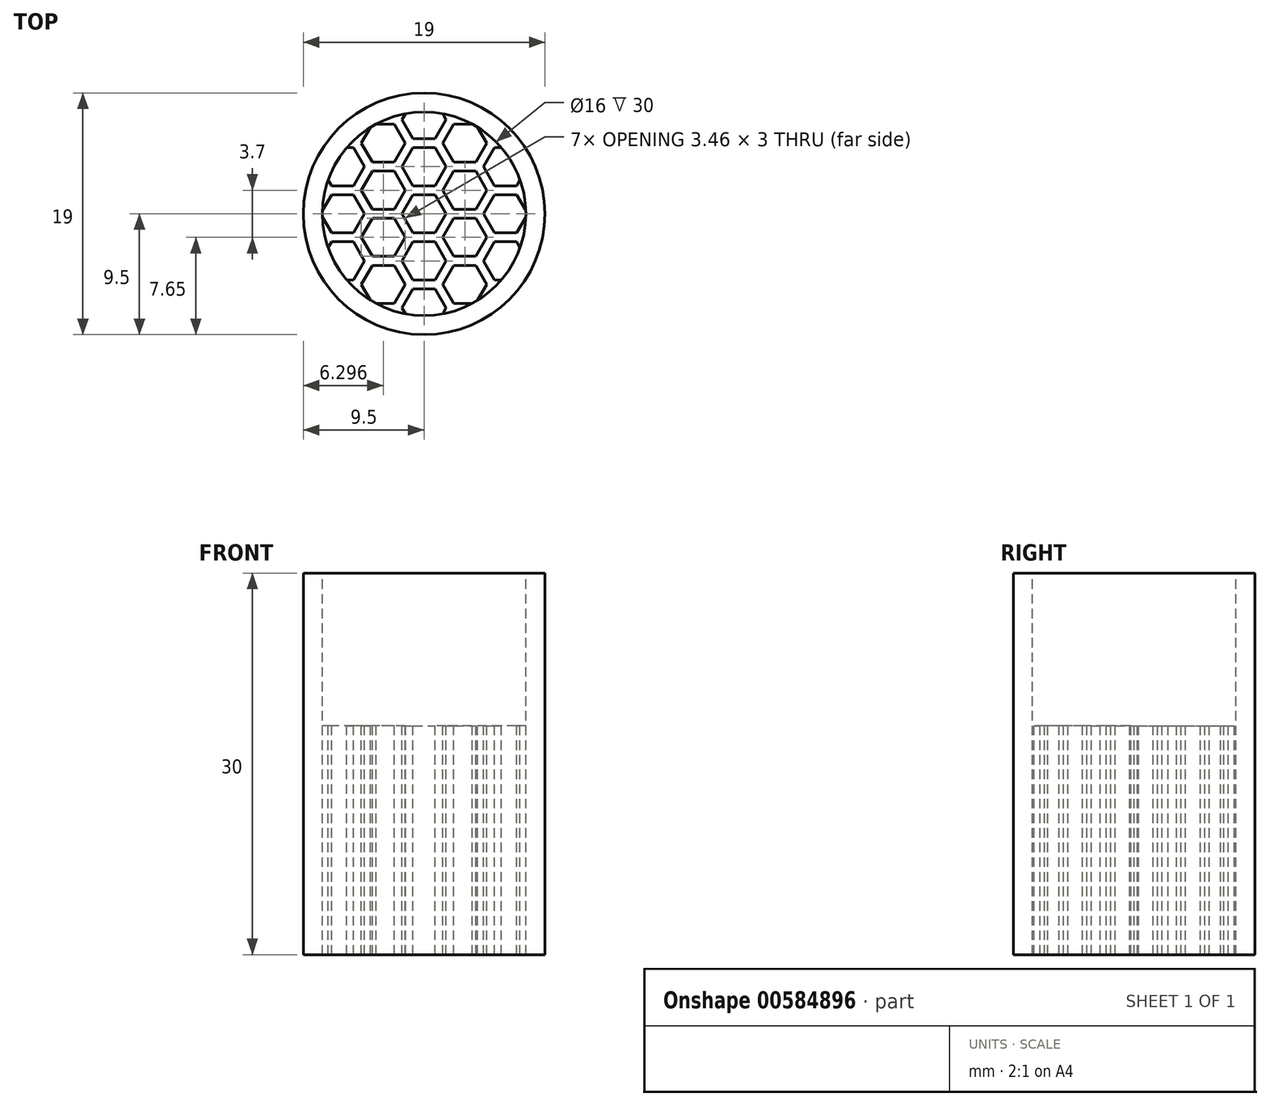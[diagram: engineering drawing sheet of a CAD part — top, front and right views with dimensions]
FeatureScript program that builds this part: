
annotation { "Feature Type Name" : "Feature", "Feature Type Description" : "" }
export const myFeature = defineFeature(function(context is Context, id is Id, definition is map)
    precondition{}
    {
        {
            var Q0;
            Q0=qCreatedBy(makeId("Top.planeOp"),FACE);
            var sketch = newSketch(context, id + "F0", { "sketchPlane" : qUnion([Q0])});
            skCircle(sketch, "E0", {"center": v(0, 0) * mm, "radius": 9.5 * mm});
            skCircle(sketch, "E1", {"center": v(0, 0) * mm, "radius": 8 * mm});
            skCircle(sketch, "E2.cCircle", {"center": v(0, 0) * mm, "radius": 1.5 * mm, "construction": true});
            skLineSegment(sketch, "E2.0", {"start": v(1.73, 0) * mm, "end": v(0.87, -1.5) * mm});
            skLineSegment(sketch, "E2.1", {"start": v(0.87, -1.5) * mm, "end": v(-0.87, -1.5) * mm});
            skLineSegment(sketch, "E2.2", {"start": v(-0.87, -1.5) * mm, "end": v(-1.73, 0) * mm});
            skLineSegment(sketch, "E2.3", {"start": v(-1.73, 0) * mm, "end": v(-0.87, 1.5) * mm});
            skLineSegment(sketch, "E2.4", {"start": v(-0.87, 1.5) * mm, "end": v(0.87, 1.5) * mm});
            skLineSegment(sketch, "E2.5", {"start": v(0.87, 1.5) * mm, "end": v(1.73, 0) * mm});
            skPoint(sketch, "E2.0.midPoint", {"position": v(1.3, -0.75) * mm});
            skCircle(sketch, "E3.cCircle", {"center": v(0, 0) * mm, "radius": 1.85 * mm, "construction": true});
            skLineSegment(sketch, "E3.0", {"start": v(2.14, 0) * mm, "end": v(1.07, -1.85) * mm});
            skLineSegment(sketch, "E3.1", {"start": v(1.07, -1.85) * mm, "end": v(-1.07, -1.85) * mm});
            skLineSegment(sketch, "E3.2", {"start": v(-1.07, -1.85) * mm, "end": v(-2.14, 0) * mm});
            skLineSegment(sketch, "E3.3", {"start": v(-2.14, 0) * mm, "end": v(-1.07, 1.85) * mm});
            skLineSegment(sketch, "E3.4", {"start": v(-1.07, 1.85) * mm, "end": v(1.07, 1.85) * mm});
            skLineSegment(sketch, "E3.5", {"start": v(1.07, 1.85) * mm, "end": v(2.14, 0) * mm});
            skPoint(sketch, "E3.0.midPoint", {"position": v(1.6, -0.92) * mm});
            skCircle(sketch, "E4.cCircle", {"center": v(0, 3.7) * mm, "radius": 1.5 * mm, "construction": true});
            skLineSegment(sketch, "E4.0", {"start": v(1.73, 3.7) * mm, "end": v(0.87, 2.2) * mm});
            skLineSegment(sketch, "E4.1", {"start": v(0.87, 2.2) * mm, "end": v(-0.87, 2.2) * mm});
            skLineSegment(sketch, "E4.2", {"start": v(-0.87, 2.2) * mm, "end": v(-1.73, 3.7) * mm});
            skLineSegment(sketch, "E4.3", {"start": v(-1.73, 3.7) * mm, "end": v(-0.87, 5.2) * mm});
            skLineSegment(sketch, "E4.4", {"start": v(-0.87, 5.2) * mm, "end": v(0.87, 5.2) * mm});
            skLineSegment(sketch, "E4.5", {"start": v(0.87, 5.2) * mm, "end": v(1.73, 3.7) * mm});
            skPoint(sketch, "E4.0.midPoint", {"position": v(1.3, 2.95) * mm});
            skCircle(sketch, "E5.cCircle", {"center": v(0, 3.7) * mm, "radius": 1.85 * mm, "construction": true});
            skLineSegment(sketch, "E5.0", {"start": v(2.14, 3.7) * mm, "end": v(1.07, 1.85) * mm});
            skLineSegment(sketch, "E5.1", {"start": v(1.07, 1.85) * mm, "end": v(-1.07, 1.85) * mm});
            skLineSegment(sketch, "E5.2", {"start": v(-1.07, 1.85) * mm, "end": v(-2.14, 3.7) * mm});
            skLineSegment(sketch, "E5.3", {"start": v(-2.14, 3.7) * mm, "end": v(-1.07, 5.55) * mm});
            skLineSegment(sketch, "E5.4", {"start": v(-1.07, 5.55) * mm, "end": v(1.07, 5.55) * mm});
            skLineSegment(sketch, "E5.5", {"start": v(1.07, 5.55) * mm, "end": v(2.14, 3.7) * mm});
            skPoint(sketch, "E5.0.midPoint", {"position": v(1.6, 2.77) * mm});
            skCircle(sketch, "E6.cCircle", {"center": v(3.2, 1.85) * mm, "radius": 1.5 * mm, "construction": true});
            skLineSegment(sketch, "E6.0", {"start": v(4.94, 1.85) * mm, "end": v(4.07, 0.35) * mm});
            skLineSegment(sketch, "E6.1", {"start": v(4.07, 0.35) * mm, "end": v(2.34, 0.35) * mm});
            skLineSegment(sketch, "E6.2", {"start": v(2.34, 0.35) * mm, "end": v(1.47, 1.85) * mm});
            skLineSegment(sketch, "E6.3", {"start": v(1.47, 1.85) * mm, "end": v(2.34, 3.35) * mm});
            skLineSegment(sketch, "E6.4", {"start": v(2.34, 3.35) * mm, "end": v(4.07, 3.35) * mm});
            skLineSegment(sketch, "E6.5", {"start": v(4.07, 3.35) * mm, "end": v(4.94, 1.85) * mm});
            skPoint(sketch, "E6.0.midPoint", {"position": v(4.5, 1.1) * mm});
            skCircle(sketch, "E7.cCircle", {"center": v(3.2, 1.85) * mm, "radius": 1.85 * mm, "construction": true});
            skLineSegment(sketch, "E7.0", {"start": v(5.34, 1.85) * mm, "end": v(4.27, 0) * mm});
            skLineSegment(sketch, "E7.1", {"start": v(4.27, 0) * mm, "end": v(2.14, 0) * mm});
            skLineSegment(sketch, "E7.2", {"start": v(2.14, 0) * mm, "end": v(1.07, 1.85) * mm});
            skLineSegment(sketch, "E7.3", {"start": v(1.07, 1.85) * mm, "end": v(2.14, 3.7) * mm});
            skLineSegment(sketch, "E7.4", {"start": v(2.14, 3.7) * mm, "end": v(4.27, 3.7) * mm});
            skLineSegment(sketch, "E7.5", {"start": v(4.27, 3.7) * mm, "end": v(5.34, 1.85) * mm});
            skPoint(sketch, "E7.0.midPoint", {"position": v(4.8, 0.93) * mm});
            skCircle(sketch, "E8.cCircle", {"center": v(3.2, -1.85) * mm, "radius": 1.5 * mm, "construction": true});
            skLineSegment(sketch, "E8.0", {"start": v(4.07, -3.35) * mm, "end": v(2.34, -3.35) * mm});
            skLineSegment(sketch, "E8.1", {"start": v(2.34, -3.35) * mm, "end": v(1.47, -1.85) * mm});
            skLineSegment(sketch, "E8.2", {"start": v(1.47, -1.85) * mm, "end": v(2.34, -0.35) * mm});
            skLineSegment(sketch, "E8.3", {"start": v(2.34, -0.35) * mm, "end": v(4.07, -0.35) * mm});
            skLineSegment(sketch, "E8.4", {"start": v(4.07, -0.35) * mm, "end": v(4.94, -1.85) * mm});
            skLineSegment(sketch, "E8.5", {"start": v(4.94, -1.85) * mm, "end": v(4.07, -3.35) * mm});
            skPoint(sketch, "E8.0.midPoint", {"position": v(3.2, -3.35) * mm});
            skCircle(sketch, "E9.cCircle", {"center": v(3.2, -1.85) * mm, "radius": 1.85 * mm, "construction": true});
            skLineSegment(sketch, "E9.0", {"start": v(4.27, -3.7) * mm, "end": v(2.14, -3.7) * mm});
            skLineSegment(sketch, "E9.1", {"start": v(2.14, -3.7) * mm, "end": v(1.07, -1.85) * mm});
            skLineSegment(sketch, "E9.2", {"start": v(1.07, -1.85) * mm, "end": v(2.14, 0) * mm});
            skLineSegment(sketch, "E9.3", {"start": v(2.14, 0) * mm, "end": v(4.27, 0) * mm});
            skLineSegment(sketch, "E9.4", {"start": v(4.27, 0) * mm, "end": v(5.34, -1.85) * mm});
            skLineSegment(sketch, "E9.5", {"start": v(5.34, -1.85) * mm, "end": v(4.27, -3.7) * mm});
            skPoint(sketch, "E9.0.midPoint", {"position": v(3.2, -3.7) * mm});
            skCircle(sketch, "E10.cCircle", {"center": v(0, -3.7) * mm, "radius": 1.5 * mm, "construction": true});
            skLineSegment(sketch, "E10.0", {"start": v(-1.73, -3.7) * mm, "end": v(-0.87, -2.2) * mm});
            skLineSegment(sketch, "E10.1", {"start": v(-0.87, -2.2) * mm, "end": v(0.87, -2.2) * mm});
            skLineSegment(sketch, "E10.2", {"start": v(0.87, -2.2) * mm, "end": v(1.73, -3.7) * mm});
            skLineSegment(sketch, "E10.3", {"start": v(1.73, -3.7) * mm, "end": v(0.87, -5.2) * mm});
            skLineSegment(sketch, "E10.4", {"start": v(0.87, -5.2) * mm, "end": v(-0.87, -5.2) * mm});
            skLineSegment(sketch, "E10.5", {"start": v(-0.87, -5.2) * mm, "end": v(-1.73, -3.7) * mm});
            skPoint(sketch, "E10.0.midPoint", {"position": v(-1.3, -2.95) * mm});
            skCircle(sketch, "E11.cCircle", {"center": v(0, -3.7) * mm, "radius": 1.85 * mm, "construction": true});
            skLineSegment(sketch, "E11.0", {"start": v(-2.14, -3.7) * mm, "end": v(-1.07, -1.85) * mm});
            skLineSegment(sketch, "E11.1", {"start": v(-1.07, -1.85) * mm, "end": v(1.07, -1.85) * mm});
            skLineSegment(sketch, "E11.2", {"start": v(1.07, -1.85) * mm, "end": v(2.14, -3.7) * mm});
            skLineSegment(sketch, "E11.3", {"start": v(2.14, -3.7) * mm, "end": v(1.07, -5.55) * mm});
            skLineSegment(sketch, "E11.4", {"start": v(1.07, -5.55) * mm, "end": v(-1.07, -5.55) * mm});
            skLineSegment(sketch, "E11.5", {"start": v(-1.07, -5.55) * mm, "end": v(-2.14, -3.7) * mm});
            skPoint(sketch, "E11.0.midPoint", {"position": v(-1.6, -2.78) * mm});
            skCircle(sketch, "E12.cCircle", {"center": v(-3.2, -1.85) * mm, "radius": 1.5 * mm, "construction": true});
            skLineSegment(sketch, "E12.0", {"start": v(-4.07, -0.35) * mm, "end": v(-2.34, -0.35) * mm});
            skLineSegment(sketch, "E12.1", {"start": v(-2.34, -0.35) * mm, "end": v(-1.47, -1.85) * mm});
            skLineSegment(sketch, "E12.2", {"start": v(-1.47, -1.85) * mm, "end": v(-2.34, -3.35) * mm});
            skLineSegment(sketch, "E12.3", {"start": v(-2.34, -3.35) * mm, "end": v(-4.07, -3.35) * mm});
            skLineSegment(sketch, "E12.4", {"start": v(-4.07, -3.35) * mm, "end": v(-4.94, -1.85) * mm});
            skLineSegment(sketch, "E12.5", {"start": v(-4.94, -1.85) * mm, "end": v(-4.07, -0.35) * mm});
            skPoint(sketch, "E12.0.midPoint", {"position": v(-3.2, -0.35) * mm});
            skCircle(sketch, "E13.cCircle", {"center": v(-3.2, -1.85) * mm, "radius": 1.85 * mm, "construction": true});
            skLineSegment(sketch, "E13.0", {"start": v(-4.27, 0) * mm, "end": v(-2.14, 0) * mm});
            skLineSegment(sketch, "E13.1", {"start": v(-2.14, 0) * mm, "end": v(-1.07, -1.85) * mm});
            skLineSegment(sketch, "E13.2", {"start": v(-1.07, -1.85) * mm, "end": v(-2.14, -3.7) * mm});
            skLineSegment(sketch, "E13.3", {"start": v(-2.14, -3.7) * mm, "end": v(-4.27, -3.7) * mm});
            skLineSegment(sketch, "E13.4", {"start": v(-4.27, -3.7) * mm, "end": v(-5.34, -1.85) * mm});
            skLineSegment(sketch, "E13.5", {"start": v(-5.34, -1.85) * mm, "end": v(-4.27, 0) * mm});
            skPoint(sketch, "E13.0.midPoint", {"position": v(-3.2, 0) * mm});
            skCircle(sketch, "E14.cCircle", {"center": v(-3.2, 1.85) * mm, "radius": 1.5 * mm, "construction": true});
            skLineSegment(sketch, "E14.0", {"start": v(-2.34, 3.35) * mm, "end": v(-1.47, 1.85) * mm});
            skLineSegment(sketch, "E14.1", {"start": v(-1.47, 1.85) * mm, "end": v(-2.34, 0.35) * mm});
            skLineSegment(sketch, "E14.2", {"start": v(-2.34, 0.35) * mm, "end": v(-4.07, 0.35) * mm});
            skLineSegment(sketch, "E14.3", {"start": v(-4.07, 0.35) * mm, "end": v(-4.94, 1.85) * mm});
            skLineSegment(sketch, "E14.4", {"start": v(-4.94, 1.85) * mm, "end": v(-4.07, 3.35) * mm});
            skLineSegment(sketch, "E14.5", {"start": v(-4.07, 3.35) * mm, "end": v(-2.34, 3.35) * mm});
            skPoint(sketch, "E14.0.midPoint", {"position": v(-1.9, 2.6) * mm});
            skCircle(sketch, "E15.cCircle", {"center": v(-3.2, 1.85) * mm, "radius": 1.85 * mm, "construction": true});
            skLineSegment(sketch, "E15.0", {"start": v(-2.14, 3.7) * mm, "end": v(-1.07, 1.85) * mm});
            skLineSegment(sketch, "E15.1", {"start": v(-1.07, 1.85) * mm, "end": v(-2.14, 0) * mm});
            skLineSegment(sketch, "E15.2", {"start": v(-2.14, 0) * mm, "end": v(-4.27, 0) * mm});
            skLineSegment(sketch, "E15.3", {"start": v(-4.27, 0) * mm, "end": v(-5.34, 1.85) * mm});
            skLineSegment(sketch, "E15.4", {"start": v(-5.34, 1.85) * mm, "end": v(-4.27, 3.7) * mm});
            skLineSegment(sketch, "E15.5", {"start": v(-4.27, 3.7) * mm, "end": v(-2.14, 3.7) * mm});
            skPoint(sketch, "E15.0.midPoint", {"position": v(-1.6, 2.77) * mm});
            skCircle(sketch, "E16.cCircle", {"center": v(3.2, 5.55) * mm, "radius": 1.5 * mm, "construction": true});
            skLineSegment(sketch, "E16.0", {"start": v(4.94, 5.55) * mm, "end": v(4.07, 4.05) * mm});
            skLineSegment(sketch, "E16.1", {"start": v(4.07, 4.05) * mm, "end": v(2.34, 4.05) * mm});
            skLineSegment(sketch, "E16.2", {"start": v(2.34, 4.05) * mm, "end": v(1.47, 5.55) * mm});
            skLineSegment(sketch, "E16.3", {"start": v(1.47, 5.55) * mm, "end": v(2.34, 7.05) * mm});
            skLineSegment(sketch, "E16.4", {"start": v(2.34, 7.05) * mm, "end": v(4.07, 7.05) * mm});
            skLineSegment(sketch, "E16.5", {"start": v(4.07, 7.05) * mm, "end": v(4.94, 5.55) * mm});
            skPoint(sketch, "E16.0.midPoint", {"position": v(4.5, 4.8) * mm});
            skCircle(sketch, "E17.cCircle", {"center": v(3.2, 5.55) * mm, "radius": 1.85 * mm, "construction": true});
            skLineSegment(sketch, "E17.0", {"start": v(5.34, 5.55) * mm, "end": v(4.27, 3.7) * mm});
            skLineSegment(sketch, "E17.1", {"start": v(4.27, 3.7) * mm, "end": v(2.14, 3.7) * mm});
            skLineSegment(sketch, "E17.2", {"start": v(2.14, 3.7) * mm, "end": v(1.07, 5.55) * mm});
            skLineSegment(sketch, "E17.3", {"start": v(1.07, 5.55) * mm, "end": v(2.14, 7.4) * mm});
            skLineSegment(sketch, "E17.4", {"start": v(2.14, 7.4) * mm, "end": v(4.27, 7.4) * mm});
            skLineSegment(sketch, "E17.5", {"start": v(4.27, 7.4) * mm, "end": v(5.34, 5.55) * mm});
            skPoint(sketch, "E17.0.midPoint", {"position": v(4.8, 4.63) * mm});
            skCircle(sketch, "E18.cCircle", {"center": v(0, 7.4) * mm, "radius": 1.5 * mm, "construction": true});
            skLineSegment(sketch, "E18.0", {"start": v(1.73, 7.4) * mm, "end": v(0.87, 5.9) * mm});
            skLineSegment(sketch, "E18.1", {"start": v(0.87, 5.9) * mm, "end": v(-0.87, 5.9) * mm});
            skLineSegment(sketch, "E18.2", {"start": v(-0.87, 5.9) * mm, "end": v(-1.73, 7.4) * mm});
            skLineSegment(sketch, "E18.3", {"start": v(-1.73, 7.4) * mm, "end": v(-0.87, 8.9) * mm});
            skLineSegment(sketch, "E18.4", {"start": v(-0.87, 8.9) * mm, "end": v(0.87, 8.9) * mm});
            skLineSegment(sketch, "E18.5", {"start": v(0.87, 8.9) * mm, "end": v(1.73, 7.4) * mm});
            skPoint(sketch, "E18.0.midPoint", {"position": v(1.3, 6.65) * mm});
            skCircle(sketch, "E19.cCircle", {"center": v(0, 7.4) * mm, "radius": 1.85 * mm, "construction": true});
            skLineSegment(sketch, "E19.0", {"start": v(2.14, 7.4) * mm, "end": v(1.07, 5.55) * mm});
            skLineSegment(sketch, "E19.1", {"start": v(1.07, 5.55) * mm, "end": v(-1.07, 5.55) * mm});
            skLineSegment(sketch, "E19.2", {"start": v(-1.07, 5.55) * mm, "end": v(-2.14, 7.4) * mm});
            skLineSegment(sketch, "E19.3", {"start": v(-2.14, 7.4) * mm, "end": v(-1.07, 9.25) * mm});
            skLineSegment(sketch, "E19.4", {"start": v(-1.07, 9.25) * mm, "end": v(1.07, 9.25) * mm});
            skLineSegment(sketch, "E19.5", {"start": v(1.07, 9.25) * mm, "end": v(2.14, 7.4) * mm});
            skPoint(sketch, "E19.0.midPoint", {"position": v(1.6, 6.47) * mm});
            skCircle(sketch, "E20.cCircle", {"center": v(-3.2, 5.55) * mm, "radius": 1.5 * mm, "construction": true});
            skLineSegment(sketch, "E20.0", {"start": v(-1.47, 5.55) * mm, "end": v(-2.34, 4.05) * mm});
            skLineSegment(sketch, "E20.1", {"start": v(-2.34, 4.05) * mm, "end": v(-4.07, 4.05) * mm});
            skLineSegment(sketch, "E20.2", {"start": v(-4.07, 4.05) * mm, "end": v(-4.94, 5.55) * mm});
            skLineSegment(sketch, "E20.3", {"start": v(-4.94, 5.55) * mm, "end": v(-4.07, 7.05) * mm});
            skLineSegment(sketch, "E20.4", {"start": v(-4.07, 7.05) * mm, "end": v(-2.34, 7.05) * mm});
            skLineSegment(sketch, "E20.5", {"start": v(-2.34, 7.05) * mm, "end": v(-1.47, 5.55) * mm});
            skPoint(sketch, "E20.0.midPoint", {"position": v(-1.9, 4.8) * mm});
            skCircle(sketch, "E21.cCircle", {"center": v(-3.2, 5.55) * mm, "radius": 1.85 * mm, "construction": true});
            skLineSegment(sketch, "E21.0", {"start": v(-1.07, 5.55) * mm, "end": v(-2.14, 3.7) * mm});
            skLineSegment(sketch, "E21.1", {"start": v(-2.14, 3.7) * mm, "end": v(-4.27, 3.7) * mm});
            skLineSegment(sketch, "E21.2", {"start": v(-4.27, 3.7) * mm, "end": v(-5.34, 5.55) * mm});
            skLineSegment(sketch, "E21.3", {"start": v(-5.34, 5.55) * mm, "end": v(-4.27, 7.4) * mm});
            skLineSegment(sketch, "E21.4", {"start": v(-4.27, 7.4) * mm, "end": v(-2.14, 7.4) * mm});
            skLineSegment(sketch, "E21.5", {"start": v(-2.14, 7.4) * mm, "end": v(-1.07, 5.55) * mm});
            skPoint(sketch, "E21.0.midPoint", {"position": v(-1.6, 4.62) * mm});
            skCircle(sketch, "E22.cCircle", {"center": v(-6.4, 3.7) * mm, "radius": 1.5 * mm, "construction": true});
            skLineSegment(sketch, "E22.0", {"start": v(-7.27, 5.2) * mm, "end": v(-5.54, 5.2) * mm});
            skLineSegment(sketch, "E22.1", {"start": v(-5.54, 5.2) * mm, "end": v(-4.68, 3.7) * mm});
            skLineSegment(sketch, "E22.2", {"start": v(-4.68, 3.7) * mm, "end": v(-5.54, 2.2) * mm});
            skLineSegment(sketch, "E22.3", {"start": v(-5.54, 2.2) * mm, "end": v(-7.27, 2.2) * mm});
            skLineSegment(sketch, "E22.4", {"start": v(-7.27, 2.2) * mm, "end": v(-8.14, 3.7) * mm});
            skLineSegment(sketch, "E22.5", {"start": v(-8.14, 3.7) * mm, "end": v(-7.27, 5.2) * mm});
            skPoint(sketch, "E22.0.midPoint", {"position": v(-6.4, 5.2) * mm});
            skCircle(sketch, "E23.cCircle", {"center": v(-6.4, 3.7) * mm, "radius": 1.85 * mm, "construction": true});
            skLineSegment(sketch, "E23.0", {"start": v(-7.48, 5.55) * mm, "end": v(-5.34, 5.55) * mm});
            skLineSegment(sketch, "E23.1", {"start": v(-5.34, 5.55) * mm, "end": v(-4.27, 3.7) * mm});
            skLineSegment(sketch, "E23.2", {"start": v(-4.27, 3.7) * mm, "end": v(-5.34, 1.85) * mm});
            skLineSegment(sketch, "E23.3", {"start": v(-5.34, 1.85) * mm, "end": v(-7.48, 1.85) * mm});
            skLineSegment(sketch, "E23.4", {"start": v(-7.48, 1.85) * mm, "end": v(-8.54, 3.7) * mm});
            skLineSegment(sketch, "E23.5", {"start": v(-8.54, 3.7) * mm, "end": v(-7.48, 5.55) * mm});
            skPoint(sketch, "E23.0.midPoint", {"position": v(-6.4, 5.55) * mm});
            skCircle(sketch, "E24.cCircle", {"center": v(-6.4, 0) * mm, "radius": 1.5 * mm, "construction": true});
            skLineSegment(sketch, "E24.0", {"start": v(-8.14, 0) * mm, "end": v(-7.27, 1.5) * mm});
            skLineSegment(sketch, "E24.1", {"start": v(-7.27, 1.5) * mm, "end": v(-5.54, 1.5) * mm});
            skLineSegment(sketch, "E24.2", {"start": v(-5.54, 1.5) * mm, "end": v(-4.68, 0) * mm});
            skLineSegment(sketch, "E24.3", {"start": v(-4.68, 0) * mm, "end": v(-5.54, -1.5) * mm});
            skLineSegment(sketch, "E24.4", {"start": v(-5.54, -1.5) * mm, "end": v(-7.27, -1.5) * mm});
            skLineSegment(sketch, "E24.5", {"start": v(-7.27, -1.5) * mm, "end": v(-8.14, 0) * mm});
            skPoint(sketch, "E24.0.midPoint", {"position": v(-7.7, 0.75) * mm});
            skCircle(sketch, "E25.cCircle", {"center": v(-6.4, 0) * mm, "radius": 1.85 * mm, "construction": true});
            skLineSegment(sketch, "E25.0", {"start": v(-8.54, 0) * mm, "end": v(-7.48, 1.85) * mm});
            skLineSegment(sketch, "E25.1", {"start": v(-7.48, 1.85) * mm, "end": v(-5.34, 1.85) * mm});
            skLineSegment(sketch, "E25.2", {"start": v(-5.34, 1.85) * mm, "end": v(-4.27, 0) * mm});
            skLineSegment(sketch, "E25.3", {"start": v(-4.27, 0) * mm, "end": v(-5.34, -1.85) * mm});
            skLineSegment(sketch, "E25.4", {"start": v(-5.34, -1.85) * mm, "end": v(-7.48, -1.85) * mm});
            skLineSegment(sketch, "E25.5", {"start": v(-7.48, -1.85) * mm, "end": v(-8.54, 0) * mm});
            skPoint(sketch, "E25.0.midPoint", {"position": v(-8.01, 0.92) * mm});
            skCircle(sketch, "E26.cCircle", {"center": v(-6.4, -3.7) * mm, "radius": 1.5 * mm, "construction": true});
            skLineSegment(sketch, "E26.0", {"start": v(-8.14, -3.7) * mm, "end": v(-7.27, -2.2) * mm});
            skLineSegment(sketch, "E26.1", {"start": v(-7.27, -2.2) * mm, "end": v(-5.54, -2.2) * mm});
            skLineSegment(sketch, "E26.2", {"start": v(-5.54, -2.2) * mm, "end": v(-4.68, -3.7) * mm});
            skLineSegment(sketch, "E26.3", {"start": v(-4.68, -3.7) * mm, "end": v(-5.54, -5.2) * mm});
            skLineSegment(sketch, "E26.4", {"start": v(-5.54, -5.2) * mm, "end": v(-7.27, -5.2) * mm});
            skLineSegment(sketch, "E26.5", {"start": v(-7.27, -5.2) * mm, "end": v(-8.14, -3.7) * mm});
            skPoint(sketch, "E26.0.midPoint", {"position": v(-7.7, -2.95) * mm});
            skCircle(sketch, "E27.cCircle", {"center": v(-6.4, -3.7) * mm, "radius": 1.85 * mm, "construction": true});
            skLineSegment(sketch, "E27.0", {"start": v(-8.54, -3.7) * mm, "end": v(-7.48, -1.85) * mm});
            skLineSegment(sketch, "E27.1", {"start": v(-7.48, -1.85) * mm, "end": v(-5.34, -1.85) * mm});
            skLineSegment(sketch, "E27.2", {"start": v(-5.34, -1.85) * mm, "end": v(-4.27, -3.7) * mm});
            skLineSegment(sketch, "E27.3", {"start": v(-4.27, -3.7) * mm, "end": v(-5.34, -5.55) * mm});
            skLineSegment(sketch, "E27.4", {"start": v(-5.34, -5.55) * mm, "end": v(-7.48, -5.55) * mm});
            skLineSegment(sketch, "E27.5", {"start": v(-7.48, -5.55) * mm, "end": v(-8.54, -3.7) * mm});
            skPoint(sketch, "E27.0.midPoint", {"position": v(-8.01, -2.78) * mm});
            skCircle(sketch, "E28.cCircle", {"center": v(-3.2, -5.55) * mm, "radius": 1.5 * mm, "construction": true});
            skLineSegment(sketch, "E28.0", {"start": v(-4.07, -4.05) * mm, "end": v(-2.34, -4.05) * mm});
            skLineSegment(sketch, "E28.1", {"start": v(-2.34, -4.05) * mm, "end": v(-1.47, -5.55) * mm});
            skLineSegment(sketch, "E28.2", {"start": v(-1.47, -5.55) * mm, "end": v(-2.34, -7.05) * mm});
            skLineSegment(sketch, "E28.3", {"start": v(-2.34, -7.05) * mm, "end": v(-4.07, -7.05) * mm});
            skLineSegment(sketch, "E28.4", {"start": v(-4.07, -7.05) * mm, "end": v(-4.94, -5.55) * mm});
            skLineSegment(sketch, "E28.5", {"start": v(-4.94, -5.55) * mm, "end": v(-4.07, -4.05) * mm});
            skPoint(sketch, "E28.0.midPoint", {"position": v(-3.2, -4.05) * mm});
            skCircle(sketch, "E29.cCircle", {"center": v(-3.2, -5.55) * mm, "radius": 1.85 * mm, "construction": true});
            skLineSegment(sketch, "E29.0", {"start": v(-4.27, -3.7) * mm, "end": v(-2.14, -3.7) * mm});
            skLineSegment(sketch, "E29.1", {"start": v(-2.14, -3.7) * mm, "end": v(-1.07, -5.55) * mm});
            skLineSegment(sketch, "E29.2", {"start": v(-1.07, -5.55) * mm, "end": v(-2.14, -7.4) * mm});
            skLineSegment(sketch, "E29.3", {"start": v(-2.14, -7.4) * mm, "end": v(-4.27, -7.4) * mm});
            skLineSegment(sketch, "E29.4", {"start": v(-4.27, -7.4) * mm, "end": v(-5.34, -5.55) * mm});
            skLineSegment(sketch, "E29.5", {"start": v(-5.34, -5.55) * mm, "end": v(-4.27, -3.7) * mm});
            skPoint(sketch, "E29.0.midPoint", {"position": v(-3.2, -3.7) * mm});
            skCircle(sketch, "E30.cCircle", {"center": v(0, -7.4) * mm, "radius": 1.5 * mm, "construction": true});
            skLineSegment(sketch, "E30.0", {"start": v(-1.73, -7.4) * mm, "end": v(-0.87, -5.9) * mm});
            skLineSegment(sketch, "E30.1", {"start": v(-0.87, -5.9) * mm, "end": v(0.87, -5.9) * mm});
            skLineSegment(sketch, "E30.2", {"start": v(0.87, -5.9) * mm, "end": v(1.73, -7.4) * mm});
            skLineSegment(sketch, "E30.3", {"start": v(1.73, -7.4) * mm, "end": v(0.87, -8.9) * mm});
            skLineSegment(sketch, "E30.4", {"start": v(0.87, -8.9) * mm, "end": v(-0.87, -8.9) * mm});
            skLineSegment(sketch, "E30.5", {"start": v(-0.87, -8.9) * mm, "end": v(-1.73, -7.4) * mm});
            skPoint(sketch, "E30.0.midPoint", {"position": v(-1.3, -6.65) * mm});
            skCircle(sketch, "E31.cCircle", {"center": v(0, -7.4) * mm, "radius": 1.85 * mm, "construction": true});
            skLineSegment(sketch, "E31.0", {"start": v(-2.14, -7.4) * mm, "end": v(-1.07, -5.55) * mm});
            skLineSegment(sketch, "E31.1", {"start": v(-1.07, -5.55) * mm, "end": v(1.07, -5.55) * mm});
            skLineSegment(sketch, "E31.2", {"start": v(1.07, -5.55) * mm, "end": v(2.14, -7.4) * mm});
            skLineSegment(sketch, "E31.3", {"start": v(2.14, -7.4) * mm, "end": v(1.07, -9.25) * mm});
            skLineSegment(sketch, "E31.4", {"start": v(1.07, -9.25) * mm, "end": v(-1.07, -9.25) * mm});
            skLineSegment(sketch, "E31.5", {"start": v(-1.07, -9.25) * mm, "end": v(-2.14, -7.4) * mm});
            skPoint(sketch, "E31.0.midPoint", {"position": v(-1.6, -6.48) * mm});
            skCircle(sketch, "E32.cCircle", {"center": v(3.2, -5.55) * mm, "radius": 1.5 * mm, "construction": true});
            skLineSegment(sketch, "E32.0", {"start": v(4.94, -5.55) * mm, "end": v(4.07, -7.05) * mm});
            skLineSegment(sketch, "E32.1", {"start": v(4.07, -7.05) * mm, "end": v(2.34, -7.05) * mm});
            skLineSegment(sketch, "E32.2", {"start": v(2.34, -7.05) * mm, "end": v(1.47, -5.55) * mm});
            skLineSegment(sketch, "E32.3", {"start": v(1.47, -5.55) * mm, "end": v(2.34, -4.05) * mm});
            skLineSegment(sketch, "E32.4", {"start": v(2.34, -4.05) * mm, "end": v(4.07, -4.05) * mm});
            skLineSegment(sketch, "E32.5", {"start": v(4.07, -4.05) * mm, "end": v(4.94, -5.55) * mm});
            skPoint(sketch, "E32.0.midPoint", {"position": v(4.5, -6.3) * mm});
            skCircle(sketch, "E33.cCircle", {"center": v(3.2, -5.55) * mm, "radius": 1.85 * mm, "construction": true});
            skLineSegment(sketch, "E33.0", {"start": v(5.34, -5.55) * mm, "end": v(4.27, -7.4) * mm});
            skLineSegment(sketch, "E33.1", {"start": v(4.27, -7.4) * mm, "end": v(2.14, -7.4) * mm});
            skLineSegment(sketch, "E33.2", {"start": v(2.14, -7.4) * mm, "end": v(1.07, -5.55) * mm});
            skLineSegment(sketch, "E33.3", {"start": v(1.07, -5.55) * mm, "end": v(2.14, -3.7) * mm});
            skLineSegment(sketch, "E33.4", {"start": v(2.14, -3.7) * mm, "end": v(4.27, -3.7) * mm});
            skLineSegment(sketch, "E33.5", {"start": v(4.27, -3.7) * mm, "end": v(5.34, -5.55) * mm});
            skPoint(sketch, "E33.0.midPoint", {"position": v(4.8, -6.48) * mm});
            skCircle(sketch, "E34.cCircle", {"center": v(6.4, -3.7) * mm, "radius": 1.5 * mm, "construction": true});
            skLineSegment(sketch, "E34.0", {"start": v(8.14, -3.7) * mm, "end": v(7.27, -5.2) * mm});
            skLineSegment(sketch, "E34.1", {"start": v(7.27, -5.2) * mm, "end": v(5.54, -5.2) * mm});
            skLineSegment(sketch, "E34.2", {"start": v(5.54, -5.2) * mm, "end": v(4.68, -3.7) * mm});
            skLineSegment(sketch, "E34.3", {"start": v(4.68, -3.7) * mm, "end": v(5.54, -2.2) * mm});
            skLineSegment(sketch, "E34.4", {"start": v(5.54, -2.2) * mm, "end": v(7.27, -2.2) * mm});
            skLineSegment(sketch, "E34.5", {"start": v(7.27, -2.2) * mm, "end": v(8.14, -3.7) * mm});
            skPoint(sketch, "E34.0.midPoint", {"position": v(7.7, -4.45) * mm});
            skCircle(sketch, "E35.cCircle", {"center": v(6.4, -3.7) * mm, "radius": 1.85 * mm, "construction": true});
            skLineSegment(sketch, "E35.0", {"start": v(8.54, -3.7) * mm, "end": v(7.48, -5.55) * mm});
            skLineSegment(sketch, "E35.1", {"start": v(7.48, -5.55) * mm, "end": v(5.34, -5.55) * mm});
            skLineSegment(sketch, "E35.2", {"start": v(5.34, -5.55) * mm, "end": v(4.27, -3.7) * mm});
            skLineSegment(sketch, "E35.3", {"start": v(4.27, -3.7) * mm, "end": v(5.34, -1.85) * mm});
            skLineSegment(sketch, "E35.4", {"start": v(5.34, -1.85) * mm, "end": v(7.48, -1.85) * mm});
            skLineSegment(sketch, "E35.5", {"start": v(7.48, -1.85) * mm, "end": v(8.54, -3.7) * mm});
            skPoint(sketch, "E35.0.midPoint", {"position": v(8.01, -4.62) * mm});
            skCircle(sketch, "E36.cCircle", {"center": v(6.4, 0) * mm, "radius": 1.5 * mm, "construction": true});
            skLineSegment(sketch, "E36.0", {"start": v(8.14, 0) * mm, "end": v(7.27, -1.5) * mm});
            skLineSegment(sketch, "E36.1", {"start": v(7.27, -1.5) * mm, "end": v(5.54, -1.5) * mm});
            skLineSegment(sketch, "E36.2", {"start": v(5.54, -1.5) * mm, "end": v(4.68, 0) * mm});
            skLineSegment(sketch, "E36.3", {"start": v(4.68, 0) * mm, "end": v(5.54, 1.5) * mm});
            skLineSegment(sketch, "E36.4", {"start": v(5.54, 1.5) * mm, "end": v(7.27, 1.5) * mm});
            skLineSegment(sketch, "E36.5", {"start": v(7.27, 1.5) * mm, "end": v(8.14, 0) * mm});
            skPoint(sketch, "E36.0.midPoint", {"position": v(7.7, -0.75) * mm});
            skCircle(sketch, "E37.cCircle", {"center": v(6.4, 0) * mm, "radius": 1.85 * mm, "construction": true});
            skLineSegment(sketch, "E37.0", {"start": v(8.54, 0) * mm, "end": v(7.48, -1.85) * mm});
            skLineSegment(sketch, "E37.1", {"start": v(7.48, -1.85) * mm, "end": v(5.34, -1.85) * mm});
            skLineSegment(sketch, "E37.2", {"start": v(5.34, -1.85) * mm, "end": v(4.27, 0) * mm});
            skLineSegment(sketch, "E37.3", {"start": v(4.27, 0) * mm, "end": v(5.34, 1.85) * mm});
            skLineSegment(sketch, "E37.4", {"start": v(5.34, 1.85) * mm, "end": v(7.48, 1.85) * mm});
            skLineSegment(sketch, "E37.5", {"start": v(7.48, 1.85) * mm, "end": v(8.54, 0) * mm});
            skPoint(sketch, "E37.0.midPoint", {"position": v(8.01, -0.92) * mm});
            skCircle(sketch, "E38.cCircle", {"center": v(6.4, 3.7) * mm, "radius": 1.5 * mm, "construction": true});
            skLineSegment(sketch, "E38.0", {"start": v(8.14, 3.7) * mm, "end": v(7.27, 2.2) * mm});
            skLineSegment(sketch, "E38.1", {"start": v(7.27, 2.2) * mm, "end": v(5.54, 2.2) * mm});
            skLineSegment(sketch, "E38.2", {"start": v(5.54, 2.2) * mm, "end": v(4.68, 3.7) * mm});
            skLineSegment(sketch, "E38.3", {"start": v(4.68, 3.7) * mm, "end": v(5.54, 5.2) * mm});
            skLineSegment(sketch, "E38.4", {"start": v(5.54, 5.2) * mm, "end": v(7.27, 5.2) * mm});
            skLineSegment(sketch, "E38.5", {"start": v(7.27, 5.2) * mm, "end": v(8.14, 3.7) * mm});
            skPoint(sketch, "E38.0.midPoint", {"position": v(7.7, 2.95) * mm});
            skCircle(sketch, "E39.cCircle", {"center": v(6.4, 3.7) * mm, "radius": 1.85 * mm, "construction": true});
            skLineSegment(sketch, "E39.0", {"start": v(8.54, 3.7) * mm, "end": v(7.48, 1.85) * mm});
            skLineSegment(sketch, "E39.1", {"start": v(7.48, 1.85) * mm, "end": v(5.34, 1.85) * mm});
            skLineSegment(sketch, "E39.2", {"start": v(5.34, 1.85) * mm, "end": v(4.27, 3.7) * mm});
            skLineSegment(sketch, "E39.3", {"start": v(4.27, 3.7) * mm, "end": v(5.34, 5.55) * mm});
            skLineSegment(sketch, "E39.4", {"start": v(5.34, 5.55) * mm, "end": v(7.48, 5.55) * mm});
            skLineSegment(sketch, "E39.5", {"start": v(7.48, 5.55) * mm, "end": v(8.54, 3.7) * mm});
            skPoint(sketch, "E39.0.midPoint", {"position": v(8.01, 2.78) * mm});
            skSolve(sketch);
        }
        {
            var Q0;
            Q0=makeQuery(id+"F0.imprint","IMPRINT",FACE,{"disambiguationData":[TD([[makeQuery(id+"F0.imprint","IMPRINT",EDGE,{"derivedFrom":sQuery(id+"F0.wireOp",EDGE,"E14.0")}),1.0]])]});
            var Q1;
            Q1=makeQuery(id+"F0.imprint","IMPRINT",FACE,{"disambiguationData":[TD([[makeQuery(id+"F0.imprint","IMPRINT",EDGE,{"derivedFrom":sQuery(id+"F0.wireOp",EDGE,"E0")}),1.0]])]});
            var Q2;
            Q2=makeQuery(id+"F0.imprint","IMPRINT",FACE,{"disambiguationData":[TD([[makeQuery(id+"F0.imprint","IMPRINT",EDGE,{"derivedFrom":sQuery(id+"F0.wireOp",EDGE,"E20.0")}),1.0]])]});
            var Q3;
            {var subQ0=sQuery(id+"F0.wireOp",EDGE,"E21.3");var subQ1=sQuery(id+"F0.wireOp",EDGE,"E1");var subQ2=makeQuery(id+"F0.imprint","INTERSECT",VERTEX,{"derivedFrom":[subQ1,subQ0]});Q3=makeQuery(id+"F0.imprint","IMPRINT",FACE,{"disambiguationData":[TD([[makeQuery(id+"F0.imprint","IMPRINT",EDGE,{"disambiguationData":[TD([[subQ2,-1.0]])],"derivedFrom":subQ1}),1.0]])]});}
            var Q4;
            {var subQ0=sQuery(id+"F0.wireOp",EDGE,"E22.5");Q4=makeQuery(id+"F0.imprint","IMPRINT",FACE,{"disambiguationData":[TD([[makeQuery(id+"F0.imprint","IMPRINT",EDGE,{"derivedFrom":subQ0}),1.0]])]});}
            var Q5;
            {var subQ9=sQuery(id+"F0.wireOp",EDGE,"E22.1");Q5=makeQuery(id+"F0.imprint","IMPRINT",FACE,{"disambiguationData":[TD([[makeQuery(id+"F0.imprint","IMPRINT",EDGE,{"derivedFrom":subQ9}),1.0]])]});}
            var Q6;
            {var subQ0=sQuery(id+"F0.wireOp",EDGE,"E23.4");var subQ1=sQuery(id+"F0.wireOp",EDGE,"E1");var subQ2=makeQuery(id+"F0.imprint","INTERSECT",VERTEX,{"derivedFrom":[subQ1,subQ0]});Q6=makeQuery(id+"F0.imprint","IMPRINT",FACE,{"disambiguationData":[TD([[makeQuery(id+"F0.imprint","IMPRINT",EDGE,{"disambiguationData":[TD([[subQ2,-1.0]])],"derivedFrom":subQ1}),1.0]])]});}
            var Q7;
            {var subQ7=sQuery(id+"F0.wireOp",EDGE,"E24.1");Q7=makeQuery(id+"F0.imprint","IMPRINT",FACE,{"disambiguationData":[TD([[makeQuery(id+"F0.imprint","IMPRINT",EDGE,{"derivedFrom":subQ7}),1.0]])]});}
            var Q8;
            {var subQ3=sQuery(id+"F0.wireOp",EDGE,"E1");var subQ8=sQuery(id+"F0.wireOp",EDGE,"E25.0");var subQ9=makeQuery(id+"F0.imprint","INTERSECT",VERTEX,{"derivedFrom":[subQ3,subQ8]});Q8=makeQuery(id+"F0.imprint","IMPRINT",FACE,{"disambiguationData":[TD([[makeQuery(id+"F0.imprint","IMPRINT",EDGE,{"disambiguationData":[TD([[subQ9,-1.0]])],"derivedFrom":subQ3}),-1.0]])]});}
            var Q9;
            Q9=makeQuery(id+"F0.imprint","IMPRINT",FACE,{"disambiguationData":[TD([[makeQuery(id+"F0.imprint","IMPRINT",EDGE,{"derivedFrom":sQuery(id+"F0.wireOp",EDGE,"E12.0")}),1.0]])]});
            var Q10;
            {var subQ0=sQuery(id+"F0.wireOp",EDGE,"E25.5");var subQ1=sQuery(id+"F0.wireOp",EDGE,"E1");var subQ2=makeQuery(id+"F0.imprint","INTERSECT",VERTEX,{"derivedFrom":[subQ1,subQ0]});Q10=makeQuery(id+"F0.imprint","IMPRINT",FACE,{"disambiguationData":[TD([[makeQuery(id+"F0.imprint","IMPRINT",EDGE,{"disambiguationData":[TD([[subQ2,-1.0]])],"derivedFrom":subQ1}),1.0]])]});}
            var Q11;
            {var subQ11=sQuery(id+"F0.wireOp",EDGE,"E26.1");Q11=makeQuery(id+"F0.imprint","IMPRINT",FACE,{"disambiguationData":[TD([[makeQuery(id+"F0.imprint","IMPRINT",EDGE,{"derivedFrom":subQ11}),1.0]])]});}
            var Q12;
            {var subQ0=sQuery(id+"F0.wireOp",EDGE,"E26.5");Q12=makeQuery(id+"F0.imprint","IMPRINT",FACE,{"disambiguationData":[TD([[makeQuery(id+"F0.imprint","IMPRINT",EDGE,{"derivedFrom":subQ0}),1.0]])]});}
            var Q13;
            {var subQ0=sQuery(id+"F0.wireOp",EDGE,"E27.4");var subQ1=sQuery(id+"F0.wireOp",EDGE,"E1");var subQ2=makeQuery(id+"F0.imprint","INTERSECT",VERTEX,{"derivedFrom":[subQ1,subQ0]});Q13=makeQuery(id+"F0.imprint","IMPRINT",FACE,{"disambiguationData":[TD([[makeQuery(id+"F0.imprint","IMPRINT",EDGE,{"disambiguationData":[TD([[subQ2,-1.0]])],"derivedFrom":subQ1}),1.0]])]});}
            var Q14;
            Q14=makeQuery(id+"F0.imprint","IMPRINT",FACE,{"disambiguationData":[TD([[makeQuery(id+"F0.imprint","IMPRINT",EDGE,{"derivedFrom":sQuery(id+"F0.wireOp",EDGE,"E28.0")}),1.0]])]});
            var Q15;
            {var subQ3=sQuery(id+"F0.wireOp",EDGE,"E1");var subQ8=sQuery(id+"F0.wireOp",EDGE,"E29.4");var subQ9=makeQuery(id+"F0.imprint","INTERSECT",VERTEX,{"derivedFrom":[subQ3,subQ8]});Q15=makeQuery(id+"F0.imprint","IMPRINT",FACE,{"disambiguationData":[TD([[makeQuery(id+"F0.imprint","IMPRINT",EDGE,{"disambiguationData":[TD([[subQ9,-1.0]])],"derivedFrom":subQ3}),-1.0]])]});}
            var Q16;
            {var subQ5=sQuery(id+"F0.wireOp",EDGE,"E26.5");Q16=makeQuery(id+"F0.imprint","IMPRINT",FACE,{"disambiguationData":[TD([[makeQuery(id+"F0.imprint","IMPRINT",EDGE,{"derivedFrom":subQ5}),-1.0]])]});}
            var Q17;
            {var subQ5=sQuery(id+"F0.wireOp",EDGE,"E22.5");Q17=makeQuery(id+"F0.imprint","IMPRINT",FACE,{"disambiguationData":[TD([[makeQuery(id+"F0.imprint","IMPRINT",EDGE,{"derivedFrom":subQ5}),-1.0]])]});}
            var Q18;
            {var subQ5=sQuery(id+"F0.wireOp",EDGE,"E18.4");Q18=makeQuery(id+"F0.imprint","IMPRINT",FACE,{"disambiguationData":[TD([[makeQuery(id+"F0.imprint","IMPRINT",EDGE,{"derivedFrom":subQ5}),-1.0]])]});}
            var Q19;
            {var subQ0=sQuery(id+"F0.wireOp",EDGE,"E18.4");Q19=makeQuery(id+"F0.imprint","IMPRINT",FACE,{"disambiguationData":[TD([[makeQuery(id+"F0.imprint","IMPRINT",EDGE,{"derivedFrom":subQ0}),1.0]])]});}
            var Q20;
            {var subQ0=sQuery(id+"F0.wireOp",EDGE,"E19.3");var subQ1=sQuery(id+"F0.wireOp",EDGE,"E1");var subQ2=makeQuery(id+"F0.imprint","INTERSECT",VERTEX,{"derivedFrom":[subQ1,subQ0]});Q20=makeQuery(id+"F0.imprint","IMPRINT",FACE,{"disambiguationData":[TD([[makeQuery(id+"F0.imprint","IMPRINT",EDGE,{"disambiguationData":[TD([[subQ2,-1.0]])],"derivedFrom":subQ1}),1.0]])]});}
            var Q21;
            {var subQ9=sQuery(id+"F0.wireOp",EDGE,"E18.0");Q21=makeQuery(id+"F0.imprint","IMPRINT",FACE,{"disambiguationData":[TD([[makeQuery(id+"F0.imprint","IMPRINT",EDGE,{"derivedFrom":subQ9}),1.0]])]});}
            var Q22;
            {var subQ0=sQuery(id+"F0.wireOp",EDGE,"E17.4");var subQ1=sQuery(id+"F0.wireOp",EDGE,"E1");var subQ2=makeQuery(id+"F0.imprint","INTERSECT",VERTEX,{"derivedFrom":[subQ1,subQ0]});Q22=makeQuery(id+"F0.imprint","IMPRINT",FACE,{"disambiguationData":[TD([[makeQuery(id+"F0.imprint","IMPRINT",EDGE,{"disambiguationData":[TD([[subQ2,-1.0]])],"derivedFrom":subQ1}),1.0]])]});}
            var Q23;
            {var subQ3=sQuery(id+"F0.wireOp",EDGE,"E1");var subQ8=sQuery(id+"F0.wireOp",EDGE,"E17.5");var subQ9=makeQuery(id+"F0.imprint","INTERSECT",VERTEX,{"derivedFrom":[subQ3,subQ8]});Q23=makeQuery(id+"F0.imprint","IMPRINT",FACE,{"disambiguationData":[TD([[makeQuery(id+"F0.imprint","IMPRINT",EDGE,{"disambiguationData":[TD([[subQ9,-1.0]])],"derivedFrom":subQ3}),-1.0]])]});}
            var Q24;
            {var subQ0=sQuery(id+"F0.wireOp",EDGE,"E39.4");var subQ1=sQuery(id+"F0.wireOp",EDGE,"E1");var subQ2=makeQuery(id+"F0.imprint","INTERSECT",VERTEX,{"derivedFrom":[subQ1,subQ0]});Q24=makeQuery(id+"F0.imprint","IMPRINT",FACE,{"disambiguationData":[TD([[makeQuery(id+"F0.imprint","IMPRINT",EDGE,{"disambiguationData":[TD([[subQ2,-1.0]])],"derivedFrom":subQ1}),1.0]])]});}
            var Q25;
            {var subQ1=sQuery(id+"F0.wireOp",EDGE,"E16.0");Q25=makeQuery(id+"F0.imprint","IMPRINT",FACE,{"disambiguationData":[TD([[makeQuery(id+"F0.imprint","IMPRINT",EDGE,{"derivedFrom":subQ1}),1.0]])]});}
            var Q26;
            {var subQ0=sQuery(id+"F0.wireOp",EDGE,"E38.5");Q26=makeQuery(id+"F0.imprint","IMPRINT",FACE,{"disambiguationData":[TD([[makeQuery(id+"F0.imprint","IMPRINT",EDGE,{"derivedFrom":subQ0}),1.0]])]});}
            var Q27;
            {var subQ5=sQuery(id+"F0.wireOp",EDGE,"E38.5");Q27=makeQuery(id+"F0.imprint","IMPRINT",FACE,{"disambiguationData":[TD([[makeQuery(id+"F0.imprint","IMPRINT",EDGE,{"derivedFrom":subQ5}),-1.0]])]});}
            var Q28;
            {var subQ10=sQuery(id+"F0.wireOp",EDGE,"E38.1");Q28=makeQuery(id+"F0.imprint","IMPRINT",FACE,{"disambiguationData":[TD([[makeQuery(id+"F0.imprint","IMPRINT",EDGE,{"derivedFrom":subQ10}),1.0]])]});}
            var Q29;
            {var subQ0=sQuery(id+"F0.wireOp",EDGE,"E37.5");var subQ1=sQuery(id+"F0.wireOp",EDGE,"E1");var subQ2=makeQuery(id+"F0.imprint","INTERSECT",VERTEX,{"derivedFrom":[subQ1,subQ0]});Q29=makeQuery(id+"F0.imprint","IMPRINT",FACE,{"disambiguationData":[TD([[makeQuery(id+"F0.imprint","IMPRINT",EDGE,{"disambiguationData":[TD([[subQ2,-1.0]])],"derivedFrom":subQ1}),1.0]])]});}
            var Q30;
            {var subQ3=sQuery(id+"F0.wireOp",EDGE,"E1");var subQ8=sQuery(id+"F0.wireOp",EDGE,"E37.5");var subQ9=makeQuery(id+"F0.imprint","INTERSECT",VERTEX,{"derivedFrom":[subQ3,subQ8]});Q30=makeQuery(id+"F0.imprint","IMPRINT",FACE,{"disambiguationData":[TD([[makeQuery(id+"F0.imprint","IMPRINT",EDGE,{"disambiguationData":[TD([[subQ9,1.0]])],"derivedFrom":subQ3}),-1.0]])]});}
            var Q31;
            {var subQ11=sQuery(id+"F0.wireOp",EDGE,"E36.1");Q31=makeQuery(id+"F0.imprint","IMPRINT",FACE,{"disambiguationData":[TD([[makeQuery(id+"F0.imprint","IMPRINT",EDGE,{"derivedFrom":subQ11}),1.0]])]});}
            var Q32;
            {var subQ0=sQuery(id+"F0.wireOp",EDGE,"E35.5");var subQ1=sQuery(id+"F0.wireOp",EDGE,"E1");var subQ2=makeQuery(id+"F0.imprint","INTERSECT",VERTEX,{"derivedFrom":[subQ1,subQ0]});Q32=makeQuery(id+"F0.imprint","IMPRINT",FACE,{"disambiguationData":[TD([[makeQuery(id+"F0.imprint","IMPRINT",EDGE,{"disambiguationData":[TD([[subQ2,-1.0]])],"derivedFrom":subQ1}),1.0]])]});}
            var Q33;
            {var subQ0=sQuery(id+"F0.wireOp",EDGE,"E34.0");Q33=makeQuery(id+"F0.imprint","IMPRINT",FACE,{"disambiguationData":[TD([[makeQuery(id+"F0.imprint","IMPRINT",EDGE,{"derivedFrom":subQ0}),1.0]])]});}
            var Q34;
            {var subQ5=sQuery(id+"F0.wireOp",EDGE,"E34.0");Q34=makeQuery(id+"F0.imprint","IMPRINT",FACE,{"disambiguationData":[TD([[makeQuery(id+"F0.imprint","IMPRINT",EDGE,{"derivedFrom":subQ5}),-1.0]])]});}
            var Q35;
            {var subQ12=sQuery(id+"F0.wireOp",EDGE,"E34.2");Q35=makeQuery(id+"F0.imprint","IMPRINT",FACE,{"disambiguationData":[TD([[makeQuery(id+"F0.imprint","IMPRINT",EDGE,{"derivedFrom":subQ12}),1.0]])]});}
            var Q36;
            {var subQ0=sQuery(id+"F0.wireOp",EDGE,"E33.0");var subQ1=sQuery(id+"F0.wireOp",EDGE,"E1");var subQ2=makeQuery(id+"F0.imprint","INTERSECT",VERTEX,{"derivedFrom":[subQ1,subQ0]});Q36=makeQuery(id+"F0.imprint","IMPRINT",FACE,{"disambiguationData":[TD([[makeQuery(id+"F0.imprint","IMPRINT",EDGE,{"disambiguationData":[TD([[subQ2,-1.0]])],"derivedFrom":subQ1}),1.0]])]});}
            var Q37;
            {var subQ5=sQuery(id+"F0.wireOp",EDGE,"E32.2");Q37=makeQuery(id+"F0.imprint","IMPRINT",FACE,{"disambiguationData":[TD([[makeQuery(id+"F0.imprint","IMPRINT",EDGE,{"derivedFrom":subQ5}),1.0]])]});}
            var Q38;
            {var subQ0=sQuery(id+"F0.wireOp",EDGE,"E32.1");var subQ1=sQuery(id+"F0.wireOp",EDGE,"E1");var subQ2=makeQuery(id+"F0.imprint","INTERSECT",VERTEX,{"derivedFrom":[subQ1,subQ0]});Q38=makeQuery(id+"F0.imprint","IMPRINT",FACE,{"disambiguationData":[TD([[makeQuery(id+"F0.imprint","IMPRINT",EDGE,{"disambiguationData":[TD([[subQ2,-1.0]])],"derivedFrom":subQ1}),-1.0]])]});}
            var Q39;
            {var subQ3=sQuery(id+"F0.wireOp",EDGE,"E1");var subQ8=sQuery(id+"F0.wireOp",EDGE,"E33.1");var subQ9=makeQuery(id+"F0.imprint","INTERSECT",VERTEX,{"derivedFrom":[subQ3,subQ8]});Q39=makeQuery(id+"F0.imprint","IMPRINT",FACE,{"disambiguationData":[TD([[makeQuery(id+"F0.imprint","IMPRINT",EDGE,{"disambiguationData":[TD([[subQ9,-1.0]])],"derivedFrom":subQ3}),-1.0]])]});}
            var Q40;
            {var subQ0=sQuery(id+"F0.wireOp",EDGE,"E30.4");Q40=makeQuery(id+"F0.imprint","IMPRINT",FACE,{"disambiguationData":[TD([[makeQuery(id+"F0.imprint","IMPRINT",EDGE,{"derivedFrom":subQ0}),1.0]])]});}
            var Q41;
            {var subQ5=sQuery(id+"F0.wireOp",EDGE,"E30.4");Q41=makeQuery(id+"F0.imprint","IMPRINT",FACE,{"disambiguationData":[TD([[makeQuery(id+"F0.imprint","IMPRINT",EDGE,{"derivedFrom":subQ5}),-1.0]])]});}
            var Q42;
            {var subQ0=sQuery(id+"F0.wireOp",EDGE,"E29.3");var subQ1=sQuery(id+"F0.wireOp",EDGE,"E1");var subQ2=makeQuery(id+"F0.imprint","INTERSECT",VERTEX,{"derivedFrom":[subQ1,subQ0]});Q42=makeQuery(id+"F0.imprint","IMPRINT",FACE,{"disambiguationData":[TD([[makeQuery(id+"F0.imprint","IMPRINT",EDGE,{"disambiguationData":[TD([[subQ2,-1.0]])],"derivedFrom":subQ1}),1.0]])]});}
            var Q43;
            {var subQ0=sQuery(id+"F0.wireOp",EDGE,"E31.3");var subQ1=sQuery(id+"F0.wireOp",EDGE,"E1");var subQ2=makeQuery(id+"F0.imprint","INTERSECT",VERTEX,{"derivedFrom":[subQ1,subQ0]});Q43=makeQuery(id+"F0.imprint","IMPRINT",FACE,{"disambiguationData":[TD([[makeQuery(id+"F0.imprint","IMPRINT",EDGE,{"disambiguationData":[TD([[subQ2,-1.0]])],"derivedFrom":subQ1}),1.0]])]});}
            var Q44;
            {var subQ6=sQuery(id+"F0.wireOp",EDGE,"E30.0");Q44=makeQuery(id+"F0.imprint","IMPRINT",FACE,{"disambiguationData":[TD([[makeQuery(id+"F0.imprint","IMPRINT",EDGE,{"derivedFrom":subQ6}),1.0]])]});}
            var Q45;
            Q45=makeQuery(id+"F0.imprint","IMPRINT",FACE,{"disambiguationData":[TD([[makeQuery(id+"F0.imprint","IMPRINT",EDGE,{"derivedFrom":sQuery(id+"F0.wireOp",EDGE,"E10.0")}),1.0]])]});
            var Q46;
            Q46=makeQuery(id+"F0.imprint","IMPRINT",FACE,{"disambiguationData":[TD([[makeQuery(id+"F0.imprint","IMPRINT",EDGE,{"derivedFrom":sQuery(id+"F0.wireOp",EDGE,"E8.0")}),1.0]])]});
            var Q47;
            Q47=makeQuery(id+"F0.imprint","IMPRINT",FACE,{"disambiguationData":[TD([[makeQuery(id+"F0.imprint","IMPRINT",EDGE,{"derivedFrom":sQuery(id+"F0.wireOp",EDGE,"E6.0")}),1.0]])]});
            var Q48;
            Q48=makeQuery(id+"F0.imprint","IMPRINT",FACE,{"disambiguationData":[TD([[makeQuery(id+"F0.imprint","IMPRINT",EDGE,{"derivedFrom":sQuery(id+"F0.wireOp",EDGE,"E4.0")}),1.0]])]});
            var Q49;
            Q49=makeQuery(id+"F0.imprint","IMPRINT",FACE,{"disambiguationData":[TD([[makeQuery(id+"F0.imprint","IMPRINT",EDGE,{"derivedFrom":sQuery(id+"F0.wireOp",EDGE,"E2.0")}),1.0]])]});
            var Q50;
            {var subQ0=sQuery(id+"F0.wireOp",EDGE,"E24.0");var subQ1=sQuery(id+"F0.wireOp",EDGE,"E1");var subQ2=makeQuery(id+"F0.imprint","INTERSECT",VERTEX,{"derivedFrom":[subQ1,subQ0]});Q50=makeQuery(id+"F0.imprint","IMPRINT",FACE,{"disambiguationData":[TD([[makeQuery(id+"F0.imprint","IMPRINT",EDGE,{"disambiguationData":[TD([[subQ2,-1.0]])],"derivedFrom":subQ1}),-1.0]])]});}
            var Q51;
            {var subQ0=sQuery(id+"F0.wireOp",EDGE,"E28.4");var subQ1=sQuery(id+"F0.wireOp",EDGE,"E1");var subQ2=makeQuery(id+"F0.imprint","INTERSECT",VERTEX,{"derivedFrom":[subQ1,subQ0]});Q51=makeQuery(id+"F0.imprint","IMPRINT",FACE,{"disambiguationData":[TD([[makeQuery(id+"F0.imprint","IMPRINT",EDGE,{"disambiguationData":[TD([[subQ2,-1.0]])],"derivedFrom":subQ1}),-1.0]])]});}
            var Q52;
            {var subQ0=sQuery(id+"F0.wireOp",EDGE,"E36.5");var subQ1=sQuery(id+"F0.wireOp",EDGE,"E1");var subQ2=makeQuery(id+"F0.imprint","INTERSECT",VERTEX,{"derivedFrom":[subQ1,subQ0]});Q52=makeQuery(id+"F0.imprint","IMPRINT",FACE,{"disambiguationData":[TD([[makeQuery(id+"F0.imprint","IMPRINT",EDGE,{"disambiguationData":[TD([[subQ2,1.0]])],"derivedFrom":subQ1}),-1.0]])]});}
            var Q53;
            {var subQ0=sQuery(id+"F0.wireOp",EDGE,"E16.5");var subQ1=sQuery(id+"F0.wireOp",EDGE,"E1");var subQ2=makeQuery(id+"F0.imprint","INTERSECT",VERTEX,{"derivedFrom":[subQ1,subQ0]});Q53=makeQuery(id+"F0.imprint","IMPRINT",FACE,{"disambiguationData":[TD([[makeQuery(id+"F0.imprint","IMPRINT",EDGE,{"disambiguationData":[TD([[subQ2,-1.0]])],"derivedFrom":subQ1}),-1.0]])]});}
            var Q54;
            {var subQ3=sQuery(id+"F0.wireOp",EDGE,"E1");var subQ5=sQuery(id+"F0.wireOp",EDGE,"E21.4");var subQ6=makeQuery(id+"F0.imprint","INTERSECT",VERTEX,{"derivedFrom":[subQ3,subQ5]});Q54=makeQuery(id+"F0.imprint","IMPRINT",FACE,{"disambiguationData":[TD([[makeQuery(id+"F0.imprint","IMPRINT",EDGE,{"disambiguationData":[TD([[subQ6,-1.0]])],"derivedFrom":subQ3}),-1.0]])]});}
            var Q55;
            {var subQ0=sQuery(id+"F0.wireOp",EDGE,"E20.4");var subQ1=sQuery(id+"F0.wireOp",EDGE,"E1");var subQ2=makeQuery(id+"F0.imprint","INTERSECT",VERTEX,{"derivedFrom":[subQ1,subQ0]});Q55=makeQuery(id+"F0.imprint","IMPRINT",FACE,{"disambiguationData":[TD([[makeQuery(id+"F0.imprint","IMPRINT",EDGE,{"disambiguationData":[TD([[subQ2,-1.0]])],"derivedFrom":subQ1}),-1.0]])]});}
            extrude(context, id + "F1", {"entities" : qUnion([Q0, Q1, Q2, Q3, Q4, Q5, Q6, Q7, Q8, Q9, Q10, Q11, Q12, Q13, Q14, Q15, Q16, Q17, Q18, Q19, Q20, Q21, Q22, Q23, Q24, Q25, Q26, Q27, Q28, Q29, Q30, Q31, Q32, Q33, Q34, Q35, Q36, Q37, Q38, Q39, Q40, Q41, Q42, Q43, Q44, Q45, Q46, Q47, Q48, Q49, Q50, Q51, Q52, Q53, Q54, Q55]), "oppositeDirection" : true, "depth" : 30 * mm, "offsetDistance" : 25 * mm});
        }
        {
            var Q0;
            Q0=qCreatedBy(makeId("Top.planeOp"),FACE);
            var sketch = newSketch(context, id + "F2", { "sketchPlane" : qUnion([Q0])});
            skCircle(sketch, "E40", {"center": v(0, 0) * mm, "radius": 8 * mm});
            skSolve(sketch);
        }
        {
            var Q0;
            Q0=makeQuery(id+"F2.imprint","IMPRINT",FACE,{"disambiguationData":[TD([[makeQuery(id+"F2.imprint","IMPRINT",EDGE,{"derivedFrom":sQuery(id+"F2.wireOp",EDGE,"E40")}),1.0]])]});
            extrude(context, id + "F3", {"entities" : qUnion([Q0]), "operationType" : NewBodyOperationType.REMOVE, "oppositeDirection" : true, "depth" : 12 * mm, "offsetDistance" : 25 * mm});
        }
    });
